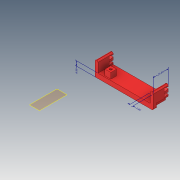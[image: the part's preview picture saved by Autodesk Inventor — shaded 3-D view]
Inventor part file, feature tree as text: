
AUTODESK INVENTOR PART (.ipt)
format: ipt  version: 2019 (Build 230136000, 136)  size: 307,712 bytes
history: native  units: mm
features: sketch x14, extrude x12, other x4, plane x4, projected_geometry x3, fillet x2
ambient origin geometry x8: Origin, YZ Plane, XZ Plane, XY Plane, X Axis, Y Axis, Z Axis, Center Point
bodies: Solid1 (feature_tree)
feature tree (39):
  other  "Annotations"
  extrude  "Extrusion1"  Depth=100.0mm
  extrude  "Extrusion2"  Depth=5.0mm
  extrude  "Extrusion3"  Depth=18.0mm TaperAngle=0.0deg
  extrude  "Extrusion4"  Depth=3.0mm
  fillet  "Fillet1"  Radius=20.0mm
  sketch  "Sketch11"  dims[d14=3.0mm d15=7.0mm]
  sketch  "Sketch12"  dims[d16=1.5mm d17=1.5mm]
  extrude  "Extrusion8"  Depth=7.0mm
  extrude  "Extrusion9"  Depth=1.5mm
  fillet  "Fillet4"  Radius=7.0mm
  extrude  "Extrusion10"  Depth=2.0mm
  extrude  "Extrusion11"  Depth=2.5mm TaperAngle=0.0deg
  sketch  "Sketch19"  dims[d41=8.0mm d42=20.0mm]
  plane  "Work Plane2"
  extrude  "Extrusion12"  TaperAngle=0.0deg  [1 undecoded]
  plane  "Work Plane3"
  extrude  "Extrusion13"  Depth=20.0mm
  extrude  "Extrusion14"  TaperAngle=0.0deg  [1 undecoded]
  plane  "Work Plane4"
  extrude  "Extrusion15"  Depth=13.0mm
  sketch  "Sketch1"  dims[d0=100.0mm d1=150.0mm]
  sketch  "Sketch3"  dims[d2=8.0mm d3=0.0mm d4=5.0mm]
  projected_geometry  "Projected Loop2"
  sketch  "Sketch4"  dims[d5=5.0mm d6=18.0mm d7=0.0mm]
  projected_geometry  "Projected Loop3"
  sketch  "Sketch6"  dims[d8=3.0mm d9=3.0mm d10=20.0mm d11=0.0mm]
  sketch  "Sketch15"  dims[d18=3.0mm d19=1.5mm d20=1.5mm d21=5.1mm d22=7.0mm]
  projected_geometry  "Projected Loop7"
  sketch  "Sketch16"  dims[d23=20.0mm d24=0.0mm d25=2.0mm]
  sketch  "Sketch17"  dims[d36=1.7mm d37=2.5mm d38=0.0mm]
  sketch  "Sketch18"  dims[d39=35.0mm d40=0.0mm]
  plane  "Work Plane1"
  sketch  "Sketch20"  dims[d43=0.0mm d44=0.0mm]
  sketch  "Sketch21"  dims[d45=25.0mm d46=13.0mm]
  sketch  "Sketch22"  dims[d47=16.0mm d48=0.0mm d49=1.0mm d50=4.2mm d51=3.5mm d52=9.0mm d53=4.2mm d54=6.0mm d55=12.0mm d56=8.0mm d57=0.0mm d60=4.3mm d61=4.3mm d62=30.8mm d64=5.0mm d65=0.0mm d66=0.0mm d67=100.0mm d69=-4.0mm d70=-2.0mm d71=10.0mm d72=0.0mm d73=-26.0mm d74=10.0mm d75=0.0mm d76=4.2mm d77=2.0mm d78=10.0mm d79=5.0mm d80=10.0mm d81=10.0mm d82=5.0mm d83=10.0mm d84=0.0mm d85=-1.5mm d86=3.15mm d87=0.0mm d88=7.0mm d89=6.218644mm d90=3.513525mm d91=8.0mm d92=0.0mm d93=10.0mm d94=26.0mm d95=2.108248mm d96=5.0mm]
  other  "Linear Dimension 1"
  other  "Linear Dimension 2"
  other  "Linear Dimension 3"
note: 2 required parameter values undecoded (feature->parameter linkage not recoverable at this tier; creation-order binding heuristic only, values carry confidence <= 0.55)
